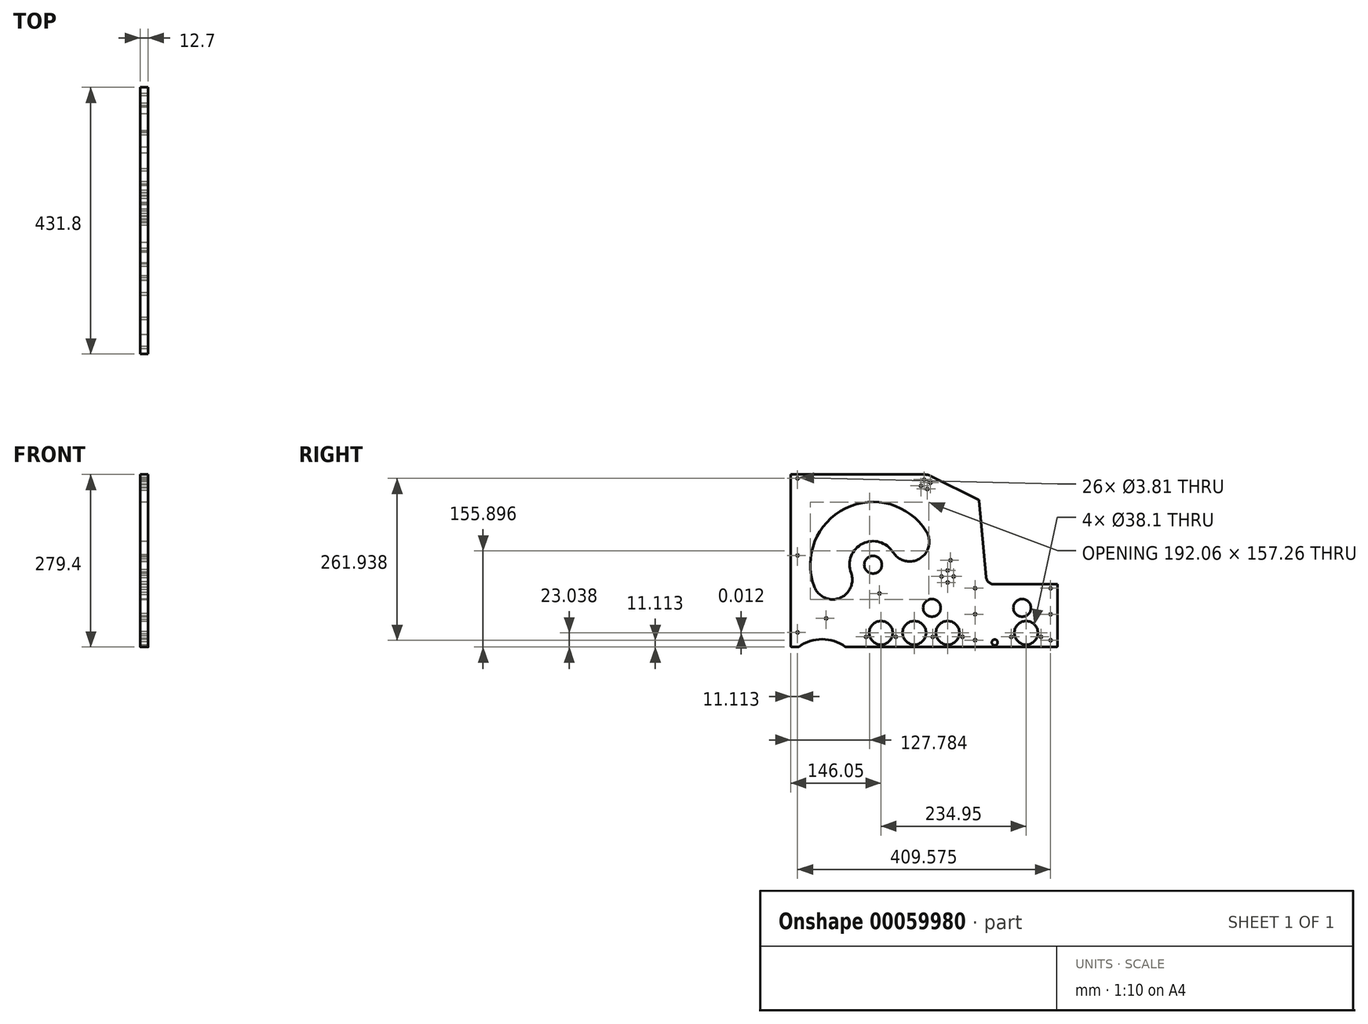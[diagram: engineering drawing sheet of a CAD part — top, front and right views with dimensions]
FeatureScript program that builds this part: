
annotation { "Feature Type Name" : "Feature", "Feature Type Description" : "" }
export const myFeature = defineFeature(function(context is Context, id is Id, definition is map)
    precondition{}
    {
        {
            var Q0;
            Q0=qCreatedBy(makeId("Right.planeOp"),FACE);
            var sketch = newSketch(context, id + "F0", { "sketchPlane" : qUnion([Q0])});
            skLineSegment(sketch, "E0.bottom", {"start": v(0, 0) * mm, "end": v(431.8, 0) * mm});
            skLineSegment(sketch, "E0.top", {"start": v(0, 355.6) * mm, "end": v(431.8, 355.6) * mm});
            skLineSegment(sketch, "E0.left", {"start": v(0, 0) * mm, "end": v(0, 355.6) * mm});
            skLineSegment(sketch, "E0.right", {"start": v(431.8, 0) * mm, "end": v(431.8, 355.6) * mm});
            skCircle(sketch, "E1", {"center": v(330.2, 7.62) * mm, "radius": 4.76 * mm});
            skCircle(sketch, "E2", {"center": v(228.6, 63.5) * mm, "radius": 14.29 * mm});
            skCircle(sketch, "E3", {"center": v(133.35, 133.35) * mm, "radius": 14.29 * mm});
            skCircle(sketch, "E4", {"center": v(374.65, 63.5) * mm, "radius": 14.29 * mm});
            skLineSegment(sketch, "E5", {"start": v(28.56, 33.11) * mm, "end": v(304.8, 161.93) * mm, "construction": true});
            skLineSegment(sketch, "E6", {"start": v(304.8, 161.93) * mm, "end": v(304.8, 33.11) * mm, "construction": true});
            skLineSegment(sketch, "E7", {"start": v(304.8, 33.11) * mm, "end": v(28.56, 33.11) * mm, "construction": true});
            skCircle(sketch, "E8", {"center": v(258.76, 140.45) * mm, "radius": 1.9 * mm});
            skCircle(sketch, "E9", {"center": v(57.33, 46.53) * mm, "radius": 1.9 * mm});
            skCircle(sketch, "E10", {"center": v(50.8, -50.8) * mm, "radius": 63.5 * mm});
            skCircle(sketch, "E11", {"center": v(143.66, 86.78) * mm, "radius": 1.9 * mm});
            skLineSegment(sketch, "E12", {"start": v(166.68, 97.52) * mm, "end": v(172.25, 86.06) * mm, "construction": true});
            skSolve(sketch);
        }
        {
            var Q0;
            Q0=makeQuery(id+"F0.imprint","IMPRINT",FACE,{"disambiguationData":[TD([[makeQuery(id+"F0.imprint","IMPRINT",EDGE,{"derivedFrom":sQuery(id+"F0.wireOp",EDGE,"E0.top")}),-1.0]])]});
            extrude(context, id + "F1", {"entities" : qUnion([Q0]), "depth" : 12.7 * mm});
        }
        {
            var Q0;
            Q0=makeQuery(id+"F1.opExtrude","CAP_FACE",FACE,{"disambiguationData":[OSD([sQuery(id+"F0.wireOp",EDGE,"E0.bottom"),sQuery(id+"F0.wireOp",EDGE,"E0.top"),sQuery(id+"F0.wireOp",EDGE,"E0.left"),sQuery(id+"F0.wireOp",EDGE,"E0.right"),sQuery(id+"F0.wireOp",EDGE,"E1"),sQuery(id+"F0.wireOp",EDGE,"E2"),sQuery(id+"F0.wireOp",EDGE,"E3"),sQuery(id+"F0.wireOp",EDGE,"E4"),sQuery(id+"F0.wireOp",EDGE,"E8"),sQuery(id+"F0.wireOp",EDGE,"E9"),sQuery(id+"F0.wireOp",EDGE,"E10")])],"isStart":false});
            var sketch = newSketch(context, id + "F2", { "sketchPlane" : qUnion([Q0])});
            skCircle(sketch, "E13", {"center": v(146.05, 23.05) * mm, "radius": 19.05 * mm});
            skCircle(sketch, "E14", {"center": v(254, 23.05) * mm, "radius": 19.05 * mm});
            skCircle(sketch, "E15", {"center": v(381, 23.04) * mm, "radius": 19.05 * mm});
            skCircle(sketch, "E16", {"center": v(200.03, 23.05) * mm, "radius": 19.05 * mm});
            skLineSegment(sketch, "E17", {"start": v(254, 23.05) * mm, "end": v(200.03, 23.05) * mm, "construction": true});
            skLineSegment(sketch, "E18", {"start": v(200.03, 23.05) * mm, "end": v(146.05, 23.05) * mm, "construction": true});
            skSolve(sketch);
        }
        {
            var Q0;
            Q0 = qSketchRegion(id + "F2", true);
            extrude(context, id + "F3", {"entities" : qUnion([Q0]), "operationType" : NewBodyOperationType.REMOVE, "endBound" : BoundingType.UP_TO_NEXT, "oppositeDirection" : true, "depth" : 25.4 * mm});
        }
        {
            var Q0;
            Q0=makeQuery(id+"F1.opExtrude","CAP_FACE",FACE,{"disambiguationData":[OSD([sQuery(id+"F0.wireOp",EDGE,"E0.bottom"),sQuery(id+"F0.wireOp",EDGE,"E0.top"),sQuery(id+"F0.wireOp",EDGE,"E0.left"),sQuery(id+"F0.wireOp",EDGE,"E0.right"),sQuery(id+"F0.wireOp",EDGE,"E1"),sQuery(id+"F0.wireOp",EDGE,"E2"),sQuery(id+"F0.wireOp",EDGE,"E3"),sQuery(id+"F0.wireOp",EDGE,"E4"),sQuery(id+"F0.wireOp",EDGE,"E8"),sQuery(id+"F0.wireOp",EDGE,"E9"),sQuery(id+"F0.wireOp",EDGE,"E10")])],"isStart":false});
            var sketch = newSketch(context, id + "F4", { "sketchPlane" : qUnion([Q0])});
            skLineSegment(sketch, "E19.bottom", {"start": v(0, 355.6) * mm, "end": v(431.8, 355.6) * mm});
            skLineSegment(sketch, "E19.left", {"start": v(0, 355.6) * mm, "end": v(0, 247.65) * mm});
            skLineSegment(sketch, "E19.right", {"start": v(431.8, 355.6) * mm, "end": v(431.8, 247.65) * mm});
            skCircle(sketch, "E20", {"center": v(133.35, 133.35) * mm, "radius": 38.1 * mm});
            skLineSegment(sketch, "E21.top", {"start": v(431.8, 101.6) * mm, "end": v(304.8, 101.6) * mm});
            skLineSegment(sketch, "E21.left", {"start": v(431.8, 247.65) * mm, "end": v(431.8, 101.6) * mm});
            skLineSegment(sketch, "E21.right", {"start": v(304.8, 238.13) * mm, "end": v(304.8, 101.6) * mm});
            skLineSegment(sketch, "E22", {"start": v(304.8, 238.13) * mm, "end": v(317.5, 101.6) * mm});
            skLineSegment(sketch, "E23", {"start": v(0, 25.4) * mm, "end": v(170.92, 139.7) * mm});
            skLineSegment(sketch, "E24.bottom", {"start": v(0, 25.4) * mm, "end": v(44.45, 25.4) * mm});
            skLineSegment(sketch, "E24.top", {"start": v(0, 279.4) * mm, "end": v(44.45, 279.4) * mm});
            skLineSegment(sketch, "E24.left", {"start": v(0, 25.4) * mm, "end": v(0, 279.4) * mm});
            skLineSegment(sketch, "E24.right", {"start": v(44.45, 25.4) * mm, "end": v(44.45, 84.16) * mm});
            skArc(sketch, "E25", {"start": v(231.78, 158.55) * mm, "mid": v(84.9, 222.65) * mm, "end": v(58.57, 64.57) * mm});
            skLineSegment(sketch, "E26", {"start": v(304.8, 238.13) * mm, "end": v(222.25, 279.4) * mm});
            skLineSegment(sketch, "E27", {"start": v(44.45, 279.4) * mm, "end": v(222.25, 279.4) * mm});
            skLineSegment(sketch, "E28", {"start": v(222.25, 279.4) * mm, "end": v(305.3, 279.4) * mm, "construction": true});
            skLineSegment(sketch, "E29.trimOffspring", {"start": v(44.45, 182.54) * mm, "end": v(44.45, 279.4) * mm});
            skLineSegment(sketch, "E30", {"start": v(231.78, 158.55) * mm, "end": v(166.8, 115.1) * mm});
            skSolve(sketch);
        }
        {
            var Q0;
            Q0=makeQuery(id+"F4.imprint","IMPRINT",FACE,{"disambiguationData":[TD([[makeQuery(id+"F4.imprint","IMPRINT",EDGE,{"derivedFrom":sQuery(id+"F4.wireOp",EDGE,"E19.bottom")}),-1.0]])]});
            var Q1;
            {var subQ6=sQuery(id+"F4.wireOp",EDGE,"E30");Q1=makeQuery(id+"F4.imprint","IMPRINT",FACE,{"disambiguationData":[TD([[makeQuery(id+"F4.imprint","IMPRINT",EDGE,{"derivedFrom":subQ6}),-1.0]])]});}
            extrude(context, id + "F5", {"entities" : qUnion([Q0, Q1]), "operationType" : NewBodyOperationType.REMOVE, "endBound" : BoundingType.UP_TO_NEXT, "oppositeDirection" : true, "depth" : 25.4 * mm});
        }
        {
            var Q0;
            Q0=makeQuery(id+"F1.opExtrude","CAP_FACE",FACE,{"disambiguationData":[OSD([sQuery(id+"F0.wireOp",EDGE,"E0.bottom"),sQuery(id+"F0.wireOp",EDGE,"E0.top"),sQuery(id+"F0.wireOp",EDGE,"E0.left"),sQuery(id+"F0.wireOp",EDGE,"E0.right"),sQuery(id+"F0.wireOp",EDGE,"E1"),sQuery(id+"F0.wireOp",EDGE,"E2"),sQuery(id+"F0.wireOp",EDGE,"E3"),sQuery(id+"F0.wireOp",EDGE,"E4"),sQuery(id+"F0.wireOp",EDGE,"E8"),sQuery(id+"F0.wireOp",EDGE,"E9"),sQuery(id+"F0.wireOp",EDGE,"E10"),sQuery(id+"F0.wireOp",EDGE,"E11")])],"isStart":false});
            var sketch = newSketch(context, id + "F6", { "sketchPlane" : qUnion([Q0])});
            skCircle(sketch, "E31", {"center": v(420.69, 11.11) * mm, "radius": 1.9 * mm});
            skCircle(sketch, "E32", {"center": v(420.69, 53.18) * mm, "radius": 1.9 * mm});
            skCircle(sketch, "E33", {"center": v(420.69, 95.25) * mm, "radius": 1.9 * mm});
            skCircle(sketch, "E34", {"center": v(298.45, 11.11) * mm, "radius": 1.9 * mm});
            skCircle(sketch, "E35", {"center": v(298.45, 95.25) * mm, "radius": 1.9 * mm});
            skCircle(sketch, "E36", {"center": v(298.45, 53.18) * mm, "radius": 1.9 * mm});
            skLineSegment(sketch, "E37", {"start": v(298.45, 11.11) * mm, "end": v(298.45, 53.18) * mm, "construction": true});
            skLineSegment(sketch, "E38", {"start": v(298.45, 95.25) * mm, "end": v(298.45, 53.18) * mm, "construction": true});
            skCircle(sketch, "E39", {"center": v(11.11, 23.81) * mm, "radius": 1.9 * mm});
            skCircle(sketch, "E40", {"center": v(122.05, 16.55) * mm, "radius": 1.9 * mm});
            skLineSegment(sketch, "E41", {"start": v(146.05, 42.1) * mm, "end": v(146.05, 4) * mm, "construction": true});
            skPoint(sketch, "E42", {"position": v(146.05, 23.05) * mm});
            skCircle(sketch, "E43.MirrorC", {"center": v(170.05, 16.55) * mm, "radius": 1.9 * mm});
            skCircle(sketch, "E44", {"center": v(230, 16.55) * mm, "radius": 1.9 * mm});
            skLineSegment(sketch, "E45", {"start": v(254, 42.1) * mm, "end": v(254, 4) * mm, "construction": true});
            skPoint(sketch, "E46", {"position": v(254, 23.05) * mm});
            skCircle(sketch, "E47.MirrorC", {"center": v(278, 16.55) * mm, "radius": 1.9 * mm});
            skLineSegment(sketch, "E48", {"start": v(381, 42.09) * mm, "end": v(381, 3.99) * mm, "construction": true});
            skCircle(sketch, "E49", {"center": v(357, 16.54) * mm, "radius": 1.9 * mm});
            skPoint(sketch, "E50", {"position": v(381, 23.04) * mm});
            skCircle(sketch, "E51.MirrorC", {"center": v(405, 16.54) * mm, "radius": 1.9 * mm});
            skCircle(sketch, "E52", {"center": v(11.11, 273.05) * mm, "radius": 1.9 * mm});
            skCircle(sketch, "E53", {"center": v(11.11, 148.43) * mm, "radius": 1.9 * mm});
            skLineSegment(sketch, "E54", {"start": v(11.11, 273.05) * mm, "end": v(11.11, 148.43) * mm, "construction": true});
            skLineSegment(sketch, "E55", {"start": v(11.11, 148.43) * mm, "end": v(11.11, 23.81) * mm, "construction": true});
            skLineSegment(sketch, "E56", {"start": v(225.6, 277.72) * mm, "end": v(218.5, 263.53) * mm, "construction": true});
            skLineSegment(sketch, "E57", {"start": v(218.5, 263.53) * mm, "end": v(218.5, 279.4) * mm, "construction": true});
            skCircle(sketch, "E58", {"center": v(218.5, 263.53) * mm, "radius": 8 * mm, "construction": true});
            skCircle(sketch, "E59", {"center": v(215.97, 271.11) * mm, "radius": 1.9 * mm});
            skLineSegment(sketch, "E60", {"start": v(215.97, 271.11) * mm, "end": v(218.5, 263.53) * mm, "construction": true});
            skLineSegment(sketch, "E61", {"start": v(218.5, 263.53) * mm, "end": v(221.03, 255.94) * mm, "construction": true});
            skLineSegment(sketch, "E62", {"start": v(218.5, 263.53) * mm, "end": v(210.91, 261) * mm, "construction": true});
            skLineSegment(sketch, "E63", {"start": v(218.5, 263.53) * mm, "end": v(226.1, 266.05) * mm, "construction": true});
            skCircle(sketch, "E64.1.0", {"center": v(210.91, 261) * mm, "radius": 1.9 * mm});
            skCircle(sketch, "E64.2.0", {"center": v(221.03, 255.94) * mm, "radius": 1.9 * mm});
            skCircle(sketch, "E64.3.0", {"center": v(226.1, 266.05) * mm, "radius": 1.9 * mm});
            skCircle(sketch, "E65", {"center": v(254, 114.3) * mm, "radius": 9.78 * mm, "construction": true});
            skCircle(sketch, "E66", {"center": v(254, 124.08) * mm, "radius": 1.9 * mm});
            skLineSegment(sketch, "E67", {"start": v(254, 124.08) * mm, "end": v(254, 114.3) * mm, "construction": true});
            skLineSegment(sketch, "E68", {"start": v(254, 114.3) * mm, "end": v(254, 124.08) * mm, "construction": true});
            skCircle(sketch, "E69.1.0", {"center": v(244.22, 114.3) * mm, "radius": 1.9 * mm});
            skCircle(sketch, "E69.2.0", {"center": v(254, 104.52) * mm, "radius": 1.9 * mm});
            skCircle(sketch, "E69.3.0", {"center": v(263.78, 114.3) * mm, "radius": 1.9 * mm});
            skSolve(sketch);
        }
        {
            var Q0;
            Q0 = qSketchRegion(id + "F6", true);
            extrude(context, id + "F7", {"entities" : qUnion([Q0]), "operationType" : NewBodyOperationType.REMOVE, "endBound" : BoundingType.UP_TO_NEXT, "oppositeDirection" : true, "depth" : 25.4 * mm});
        }
        {
            var Q0;
            Q0=makeQuery(id+"F5.boolean.opBoolean","COPY",EDGE,{"derivedFrom":makeQuery(id+"F5.opExtrude","SWEPT_EDGE",EDGE,{"disambiguationData":[OSD([sQuery(id+"F4.wireOp",EDGE,"E23"),sQuery(id+"F4.wireOp",EDGE,"E25")])]})});
            var Q1;
            Q1=makeQuery(id+"F5.boolean.opBoolean","COPY",EDGE,{"derivedFrom":makeQuery(id+"F5.opExtrude","SWEPT_EDGE",EDGE,{"disambiguationData":[OSD([sQuery(id+"F4.wireOp",EDGE,"E20"),sQuery(id+"F4.wireOp",EDGE,"E23")])]})});
            var Q2;
            Q2=makeQuery(id+"F5.boolean.opBoolean","COPY",EDGE,{"derivedFrom":makeQuery(id+"F5.opExtrude","SWEPT_EDGE",EDGE,{"disambiguationData":[OSD([sQuery(id+"F4.wireOp",EDGE,"E20"),sQuery(id+"F4.wireOp",EDGE,"E30")])]})});
            var Q3;
            Q3=makeQuery(id+"F5.boolean.opBoolean","COPY",EDGE,{"derivedFrom":makeQuery(id+"F5.opExtrude","SWEPT_EDGE",EDGE,{"disambiguationData":[OSD([sQuery(id+"F4.wireOp",EDGE,"E25"),sQuery(id+"F4.wireOp",EDGE,"E30")])]})});
            fillet(context, id + "F8", {"entities" : qUnion([Q0, Q1, Q2, Q3]), "radius" : 31.75 * mm, "tangentPropagation" : true, "allowEdgeOverflow" : false});
        }
        {
            var Q0;
            Q0=makeQuery(id+"F5.boolean.opBoolean","COPY",EDGE,{"derivedFrom":makeQuery(id+"F5.opExtrude","SWEPT_EDGE",EDGE,{"disambiguationData":[OSD([sQuery(id+"F4.wireOp",EDGE,"E26"),sQuery(id+"F4.wireOp",EDGE,"E27")])]})});
            fillet(context, id + "F9", {"entities" : qUnion([Q0]), "radius" : 25.4 * mm, "tangentPropagation" : true, "allowEdgeOverflow" : false});
        }
        {
            var Q0;
            Q0=makeQuery(id+"F5.boolean.opBoolean","COPY",EDGE,{"derivedFrom":makeQuery(id+"F5.opExtrude","SWEPT_EDGE",EDGE,{"disambiguationData":[OSD([sQuery(id+"F4.wireOp",EDGE,"E21.top"),sQuery(id+"F4.wireOp",EDGE,"E22")])]})});
            fillet(context, id + "F10", {"entities" : qUnion([Q0]), "radius" : 12.7 * mm, "tangentPropagation" : true, "allowEdgeOverflow" : false});
        }
        {
            var Q0;
            Q0=makeQuery(id+"F5.boolean.opBoolean","COPY",EDGE,{"derivedFrom":makeQuery(id+"F5.opExtrude","SWEPT_EDGE",EDGE,{"disambiguationData":[OSD([sQuery(id+"F0.wireOp",EDGE,"E0.right"),sQuery(id+"F4.wireOp",EDGE,"E21.top"),sQuery(id+"F4.wireOp",EDGE,"E21.left")])]})});
            var Q1;
            Q1=makeQuery(id+"F1.opExtrude","SWEPT_EDGE",EDGE,{"disambiguationData":[OSD([sQuery(id+"F0.wireOp",EDGE,"E0.bottom"),sQuery(id+"F0.wireOp",EDGE,"E0.right")])]});
            var Q2;
            Q2=makeQuery(id+"F1.opExtrude","SWEPT_EDGE",EDGE,{"disambiguationData":[OSD([sQuery(id+"F0.wireOp",EDGE,"E0.bottom"),sQuery(id+"F0.wireOp",EDGE,"E0.left")])]});
            var Q3;
            {var subQ0=sQuery(id+"F0.wireOp",EDGE,"E10");var subQ1=sQuery(id+"F0.wireOp",EDGE,"E0.bottom");Q3=makeQuery(id+"F1.opExtrude","SWEPT_EDGE",EDGE,{"disambiguationData":[OSD([subQ1,subQ0]),TDD([makeQuery(id+"F0.imprint","INTERSECT",VERTEX,{"disambiguationData":[OD(0.0)],"derivedFrom":[subQ1,subQ0]})])]});}
            var Q4;
            {var subQ0=sQuery(id+"F0.wireOp",EDGE,"E10");var subQ1=sQuery(id+"F0.wireOp",EDGE,"E0.bottom");Q4=makeQuery(id+"F1.opExtrude","SWEPT_EDGE",EDGE,{"disambiguationData":[OSD([subQ1,subQ0]),TDD([makeQuery(id+"F0.imprint","INTERSECT",VERTEX,{"disambiguationData":[OD(1.0)],"derivedFrom":[subQ1,subQ0]})])]});}
            var Q5;
            Q5=makeQuery(id+"F5.boolean.opBoolean","COPY",EDGE,{"derivedFrom":makeQuery(id+"F5.opExtrude","SWEPT_EDGE",EDGE,{"disambiguationData":[OSD([sQuery(id+"F4.wireOp",EDGE,"E19.left"),sQuery(id+"F4.wireOp",EDGE,"E24.top"),sQuery(id+"F4.wireOp",EDGE,"E24.left")])]})});
            var Q6;
            Q6=makeQuery(id+"F5.boolean.opBoolean","COPY",EDGE,{"derivedFrom":makeQuery(id+"F5.opExtrude","SWEPT_EDGE",EDGE,{"disambiguationData":[OSD([sQuery(id+"F4.wireOp",EDGE,"E21.right"),sQuery(id+"F4.wireOp",EDGE,"E22"),sQuery(id+"F4.wireOp",EDGE,"E26")])]})});
            fillet(context, id + "F11", {"entities" : qUnion([Q0, Q1, Q2, Q3, Q4, Q5, Q6]), "radius" : 1.59 * mm, "tangentPropagation" : true, "allowEdgeOverflow" : false});
        }
    });
